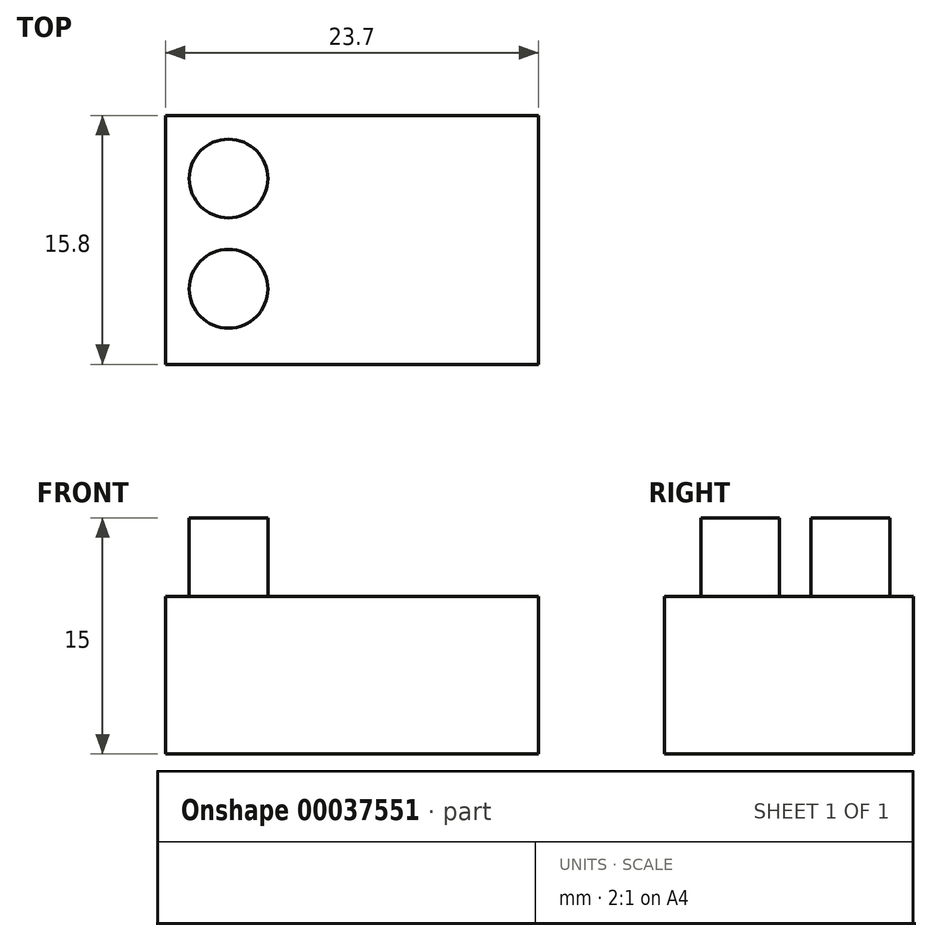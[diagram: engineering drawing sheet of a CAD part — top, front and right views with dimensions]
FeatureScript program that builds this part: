
annotation { "Feature Type Name" : "Feature", "Feature Type Description" : "" }
export const myFeature = defineFeature(function(context is Context, id is Id, definition is map)
    precondition{}
    {
        {
            var Q0;
            Q0=qCreatedBy(makeId("Top.planeOp"),FACE);
            var sketch = newSketch(context, id + "F0", { "sketchPlane" : qUnion([Q0])});
            skLineSegment(sketch, "E0.rect.bottom", {"start": v(11.85, 7.9) * mm, "end": v(-11.85, 7.9) * mm});
            skLineSegment(sketch, "E0.rect.top", {"start": v(11.85, -7.9) * mm, "end": v(-11.85, -7.9) * mm});
            skLineSegment(sketch, "E0.rect.left", {"start": v(11.85, 7.9) * mm, "end": v(11.85, -7.9) * mm});
            skLineSegment(sketch, "E0.rect.right", {"start": v(-11.85, 7.9) * mm, "end": v(-11.85, -7.9) * mm});
            skPoint(sketch, "E0.rect.middle", {"position": v(0, 0) * mm});
            skSolve(sketch);
        }
        {
            var Q0;
            Q0 = qSketchRegion(id + "F0", true);
            extrude(context, id + "F1", {"entities" : qUnion([Q0]), "depth" : 10 * mm});
        }
        {
            var Q0;
            Q0=makeQuery(id+"F1.opExtrude","CAP_FACE",FACE,{"disambiguationData":[OSD([sQuery(id+"F0.wireOp",EDGE,"E0.rect.bottom"),sQuery(id+"F0.wireOp",EDGE,"E0.rect.top"),sQuery(id+"F0.wireOp",EDGE,"E0.rect.left"),sQuery(id+"F0.wireOp",EDGE,"E0.rect.right")])],"isStart":false});
            var sketch = newSketch(context, id + "F2", { "sketchPlane" : qUnion([Q0])});
            skCircle(sketch, "E1", {"center": v(-7.85, 3.9) * mm, "radius": 2.5 * mm});
            skCircle(sketch, "E2.0.1.0", {"center": v(-7.85, -3.1) * mm, "radius": 2.5 * mm});
            skCircle(sketch, "E2.1.0.0", {"center": v(-0.4, 3.9) * mm, "radius": 2.5 * mm});
            skCircle(sketch, "E2.1.1.0", {"center": v(-0.4, -3.1) * mm, "radius": 2.5 * mm});
            skCircle(sketch, "E2.2.0.0", {"center": v(7.06, 3.9) * mm, "radius": 2.5 * mm});
            skCircle(sketch, "E2.2.1.0", {"center": v(7.06, -3.1) * mm, "radius": 2.5 * mm});
            skLineSegment(sketch, "E2.direction1", {"start": v(-7.85, 3.9) * mm, "end": v(-0.4, 3.9) * mm, "construction": true});
            skLineSegment(sketch, "E2.direction2", {"start": v(-7.85, 3.9) * mm, "end": v(-7.85, -3.1) * mm, "construction": true});
            skSolve(sketch);
        }
        {
            var Q0;
            Q0=makeQuery(id+"F2.imprint","IMPRINT",FACE,{"disambiguationData":[TD([[makeQuery(id+"F2.imprint","IMPRINT",EDGE,{"derivedFrom":sQuery(id+"F2.wireOp",EDGE,"E1")}),1.0]])]});
            var Q1;
            Q1=makeQuery(id+"F2.imprint","IMPRINT",FACE,{"disambiguationData":[TD([[makeQuery(id+"F2.imprint","IMPRINT",EDGE,{"derivedFrom":sQuery(id+"F2.wireOp",EDGE,"E2.0.1.0")}),1.0]])]});
            extrude(context, id + "F3", {"entities" : qUnion([Q0, Q1]), "operationType" : NewBodyOperationType.ADD, "depth" : 5 * mm});
        }
    });
